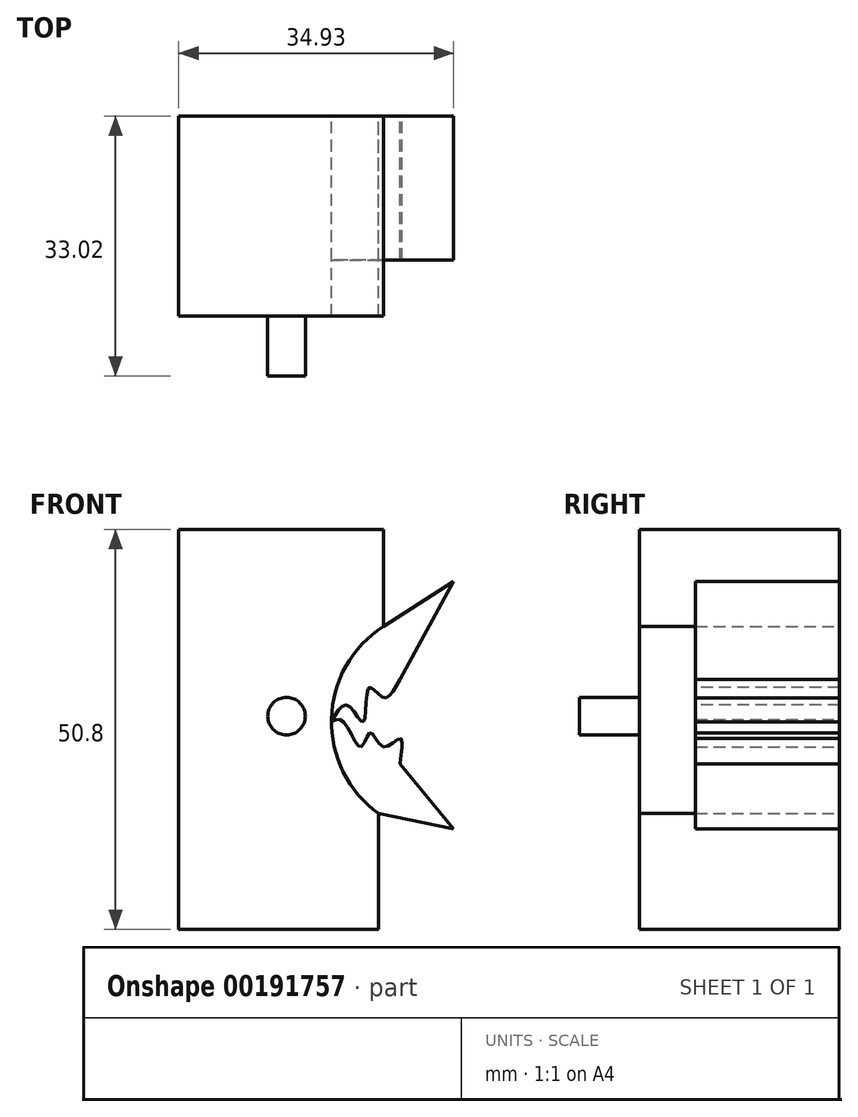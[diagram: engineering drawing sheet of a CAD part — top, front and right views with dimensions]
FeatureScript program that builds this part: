
annotation { "Feature Type Name" : "Feature", "Feature Type Description" : "" }
export const myFeature = defineFeature(function(context is Context, id is Id, definition is map)
    precondition{}
    {
        {
            var Q0;
            Q0=qCreatedBy(makeId("Front.planeOp"),FACE);
            var sketch = newSketch(context, id + "F0", { "sketchPlane" : qUnion([Q0])});
            skLineSegment(sketch, "E0", {"start": v(-50.13, 56.38) * mm, "end": v(-50.13, 5.58) * mm});
            skLineSegment(sketch, "E1", {"start": v(-50.13, 5.58) * mm, "end": v(-24.73, 5.58) * mm});
            skLineSegment(sketch, "E2", {"start": v(-24.73, 5.58) * mm, "end": v(-24.73, 20.3) * mm});
            skLineSegment(sketch, "E3", {"start": v(-50.13, 56.38) * mm, "end": v(-24.13, 56.38) * mm});
            skLineSegment(sketch, "E4", {"start": v(-24.13, 56.38) * mm, "end": v(-24.13, 44.06) * mm});
            skLineSegment(sketch, "E5", {"start": v(-24.13, 44.06) * mm, "end": v(-15.2, 49.81) * mm});
            skLineSegment(sketch, "E6", {"start": v(-15.2, 49.81) * mm, "end": v(-22.03, 37.36) * mm});
            skLineSegment(sketch, "E7", {"start": v(-24.73, 20.3) * mm, "end": v(-15.2, 18.36) * mm});
            skLineSegment(sketch, "E8", {"start": v(-15.2, 18.36) * mm, "end": v(-22.03, 26.62) * mm});
            skArc(sketch, "E9", {"start": v(-24.13, 44.06) * mm, "mid": v(-30.72, 32.34) * mm, "end": v(-24.73, 20.3) * mm});
            skFitSpline(sketch, "E10", {"points": [v(-22.03, 37.36) * mm, v(-24.13, 35.04) * mm, v(-25.94, 36.28) * mm, v(-26.69, 31.98) * mm, v(-28.64, 34.02) * mm, v(-30.73, 31.98) * mm], "startDerivative": vector(-9.7, -19.1) * mm, "endDerivative": vector(-10.17, -18.56) * mm});
            skFitSpline(sketch, "E11", {"points": [v(-22.03, 26.62) * mm, v(-22.03, 29.81) * mm, v(-24.13, 28.76) * mm, v(-25.79, 30.56) * mm, v(-26.99, 28.76) * mm, v(-29.24, 31.98) * mm, v(-30.73, 31.98) * mm], "startDerivative": vector(3.93, 25.83) * mm, "endDerivative": vector(-11.6, -5.48) * mm});
            skSolve(sketch);
        }
        {
            var Q0;
            Q0=makeQuery(id+"F0.imprint","IMPRINT",FACE,{"disambiguationData":[TD([[makeQuery(id+"F0.imprint","IMPRINT",EDGE,{"derivedFrom":sQuery(id+"F0.wireOp",EDGE,"E0")}),1.0]])]});
            var Q1;
            Q1=makeQuery(id+"F0.imprint","IMPRINT",FACE,{"disambiguationData":[TD([[makeQuery(id+"F0.imprint","IMPRINT",EDGE,{"derivedFrom":sQuery(id+"F0.wireOp",EDGE,"E0")}),1.0]])]});
            extrude(context, id + "F1", {"entities" : qUnion([Q0, Q1]), "depth" : 25.4 * mm});
        }
        {
            var Q0;
            Q0 = qSketchRegion(id + "F0", true);
            extrude(context, id + "F2", {"entities" : qUnion([Q0]), "operationType" : NewBodyOperationType.ADD, "depth" : 18.29 * mm});
        }
        {
            var Q0;
            Q0=makeQuery(id+"F1.opExtrude","CAP_FACE",FACE,{"disambiguationData":[OSD([sQuery(id+"F0.wireOp",EDGE,"E0"),sQuery(id+"F0.wireOp",EDGE,"E1"),sQuery(id+"F0.wireOp",EDGE,"E2"),sQuery(id+"F0.wireOp",EDGE,"E3"),sQuery(id+"F0.wireOp",EDGE,"E4"),sQuery(id+"F0.wireOp",EDGE,"E9")])],"isStart":false});
            var sketch = newSketch(context, id + "F3", { "sketchPlane" : qUnion([Q0])});
            skCircle(sketch, "E12", {"center": v(-36.43, 32.67) * mm, "radius": 2.39 * mm});
            skSolve(sketch);
        }
        {
            var Q0;
            Q0 = qSketchRegion(id + "F3", true);
            extrude(context, id + "F4", {"entities" : qUnion([Q0]), "operationType" : NewBodyOperationType.ADD, "depth" : 7.62 * mm});
        }
    });
